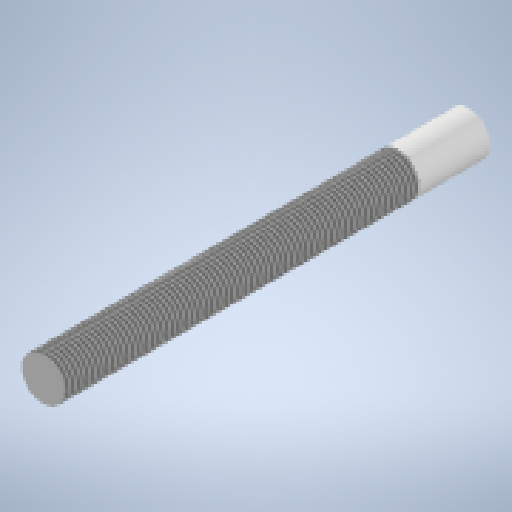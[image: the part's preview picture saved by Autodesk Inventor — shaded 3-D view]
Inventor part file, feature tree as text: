
AUTODESK INVENTOR PART (.ipt)
format: ipt  version: 2023 (Build 270158000, 158)  size: 151,552 bytes
history: native  units: mm
features: extrude x1, thread x1, sketch x1
ambient origin geometry x8: Origin, YZ Plane, XZ Plane, XY Plane, X Axis, Y Axis, Z Axis, Center Point
bodies: Solid1 (feature_tree)
feature tree (3):
  extrude  "Extrusion1"  Depth=30.0mm TaperAngle=0.0deg
  thread  "Thread1"  [1 undecoded]
  sketch  "Sketch1"  dims[d0=3.0mm d1=30.0mm d2=0.0mm d3=25.0mm d4=0.0mm]
note: 1 required parameter value undecoded (feature->parameter linkage not recoverable at this tier; creation-order binding heuristic only, values carry confidence <= 0.55)
